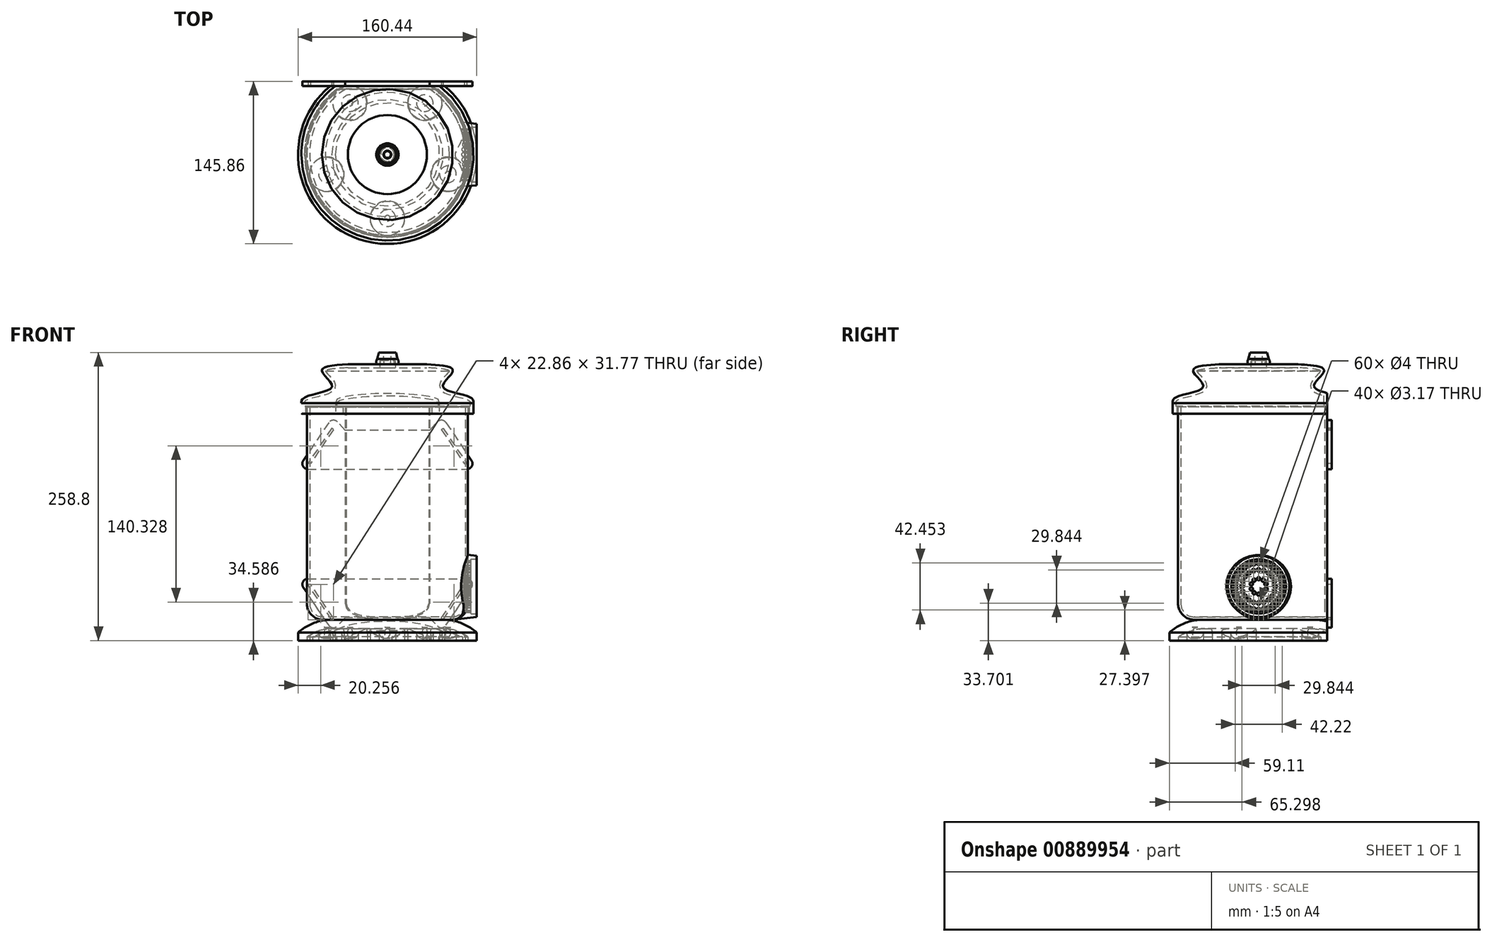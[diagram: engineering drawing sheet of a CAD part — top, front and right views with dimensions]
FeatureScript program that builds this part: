
annotation { "Feature Type Name" : "Feature", "Feature Type Description" : "" }
export const myFeature = defineFeature(function(context is Context, id is Id, definition is map)
    precondition{}
    {
        {
            var Q0;
            Q0=qCreatedBy(makeId("Top.planeOp"),FACE);
            var sketch = newSketch(context, id + "F0", { "sketchPlane" : qUnion([Q0])});
            skCircle(sketch, "E0", {"center": v(0, 0) * mm, "radius": 72.34 * mm});
            skSolve(sketch);
        }
        {
            var Q0;
            Q0=makeQuery(id+"F0.imprint","IMPRINT",FACE,{"disambiguationData":[TD([[makeQuery(id+"F0.imprint","IMPRINT",EDGE,{"derivedFrom":sQuery(id+"F0.wireOp",EDGE,"E0")}),1.0]])]});
            extrude(context, id + "F1", {"entities" : qUnion([Q0]), "depth" : 191 * mm, "offsetDistance" : 25 * mm});
        }
        {
            var Q0;
            Q0=makeQuery(id+"F1.opExtrude","CAP_EDGE",EDGE,{"disambiguationData":[OSD([sQuery(id+"F0.wireOp",EDGE,"E0")])],"isStart":true});
            fillet(context, id + "F2", {"entities" : qUnion([Q0]), "radius" : 14.5 * mm, "tangentPropagation" : true, "allowEdgeOverflow" : false});
        }
        {
            var Q0;
            Q0=qCreatedBy(makeId("Right.planeOp"),FACE);
            var sketch = newSketch(context, id + "F3", { "sketchPlane" : qUnion([Q0])});
            skLineSegment(sketch, "E1", {"start": v(0, 191.62) * mm, "end": v(0, 229.3) * mm});
            skLineSegment(sketch, "E2", {"start": v(0, 229.3) * mm, "end": v(-35.51, 229.3) * mm});
            skFitSpline(sketch, "E3", {"points": [v(-35.51, 229.3) * mm, v(-58.86, 223.46) * mm, v(-49.78, 209.2) * mm, v(-75.72, 198.82) * mm, v(-76.36, 191.62) * mm], "startDerivative": vector(-123.31, -7) * mm, "endDerivative": vector(16.64, -43.35) * mm});
            skLineSegment(sketch, "E4", {"start": v(-77.24, 194.4) * mm, "end": v(-77.24, 184.83) * mm});
            skLineSegment(sketch, "E5", {"start": v(-77.24, 184.83) * mm, "end": v(-73.36, 184.83) * mm});
            skLineSegment(sketch, "E6", {"start": v(-73.36, 184.83) * mm, "end": v(-73.36, 191.62) * mm});
            skLineSegment(sketch, "E7", {"start": v(-73.36, 191.62) * mm, "end": v(0, 191.62) * mm});
            skPoint(sketch, "E8.orphan", {"position": v(4.32, 191.62) * mm});
            skPoint(sketch, "E9.orphan", {"position": v(0, 191.04) * mm});
            skSolve(sketch);
        }
        {
            var Q0;
            Q0=makeQuery(id+"F3.imprint","IMPRINT",FACE,{"disambiguationData":[TD([[makeQuery(id+"F3.imprint","IMPRINT",EDGE,{"derivedFrom":sQuery(id+"F3.wireOp",EDGE,"E1")}),1.0]])]});
            var Q1;
            Q1=sQuery(id+"F3.wireOp",EDGE,"E1");
            revolve(context, id + "F4", {"surfaceOperationType" : NewSurfaceOperationType.NEW, "entities" : qUnion([Q0]), "axis" : qUnion([Q1]), "revolveType" : RevolveType.FULL});
        }
        {
            var Q0;
            Q0=qCreatedBy(makeId("Front.planeOp"),FACE);
            var sketch = newSketch(context, id + "F5", { "sketchPlane" : qUnion([Q0])});
            skLineSegment(sketch, "E10", {"start": v(0, 0) * mm, "end": v(-68.08, 0) * mm});
            skLineSegment(sketch, "E11", {"start": v(-68.08, 0) * mm, "end": v(-80.22, -11.61) * mm});
            skLineSegment(sketch, "E12", {"start": v(-80.22, -11.61) * mm, "end": v(-80.22, -18.75) * mm});
            skLineSegment(sketch, "E13", {"start": v(-80.22, -18.75) * mm, "end": v(0, -18.75) * mm});
            skLineSegment(sketch, "E14", {"start": v(0, -18.75) * mm, "end": v(0, 0) * mm});
            skSolve(sketch);
        }
        {
            var Q0;
            Q0=makeQuery(id+"F5.imprint","IMPRINT",FACE,{"disambiguationData":[TD([[makeQuery(id+"F5.imprint","IMPRINT",EDGE,{"derivedFrom":sQuery(id+"F5.wireOp",EDGE,"E10")}),1.0]])]});
            var Q1;
            Q1=sQuery(id+"F5.wireOp",EDGE,"E14");
            revolve(context, id + "F6", {"surfaceOperationType" : NewSurfaceOperationType.NEW, "entities" : qUnion([Q0]), "axis" : qUnion([Q1]), "revolveType" : RevolveType.FULL});
        }
        {
            var Q0;
            Q0=makeQuery(id+"F6.opRevolve","SWEPT_EDGE",EDGE,{"disambiguationData":[OSD([sQuery(id+"F5.wireOp",EDGE,"E10"),sQuery(id+"F5.wireOp",EDGE,"E11")])]});
            fillet(context, id + "F7", {"entities" : qUnion([Q0]), "radius" : 45.18 * mm, "tangentPropagation" : true, "allowEdgeOverflow" : false});
        }
        {
            var Q0;
            Q0=makeQuery(id+"F6.opRevolve","SWEPT_FACE",FACE,{"disambiguationData":[OSD([sQuery(id+"F5.wireOp",EDGE,"E13")])]});
            var sketch = newSketch(context, id + "F8", { "sketchPlane" : qUnion([Q0])});
            skCircle(sketch, "E15", {"center": v(0, 57.16) * mm, "radius": 7.5 * mm});
            skCircle(sketch, "E16.1.0", {"center": v(-54.36, 17.66) * mm, "radius": 7.5 * mm});
            skCircle(sketch, "E16.2.0", {"center": v(-33.6, -46.24) * mm, "radius": 7.5 * mm});
            skCircle(sketch, "E16.3.0", {"center": v(33.6, -46.24) * mm, "radius": 7.5 * mm});
            skCircle(sketch, "E16.4.0", {"center": v(54.36, 17.66) * mm, "radius": 7.5 * mm});
            skPoint(sketch, "E16.center", {"position": v(0, 0) * mm});
            skSolve(sketch);
        }
        {
            var Q0;
            Q0=makeQuery(id+"F8.imprint","IMPRINT",FACE,{"disambiguationData":[TD([[makeQuery(id+"F8.imprint","IMPRINT",EDGE,{"derivedFrom":sQuery(id+"F8.wireOp",EDGE,"E15")}),1.0]])]});
            var Q1;
            Q1=makeQuery(id+"F8.imprint","IMPRINT",FACE,{"disambiguationData":[TD([[makeQuery(id+"F8.imprint","IMPRINT",EDGE,{"derivedFrom":sQuery(id+"F8.wireOp",EDGE,"E16.4.0")}),1.0]])]});
            var Q2;
            Q2=makeQuery(id+"F8.imprint","IMPRINT",FACE,{"disambiguationData":[TD([[makeQuery(id+"F8.imprint","IMPRINT",EDGE,{"derivedFrom":sQuery(id+"F8.wireOp",EDGE,"E16.3.0")}),1.0]])]});
            var Q3;
            Q3=makeQuery(id+"F8.imprint","IMPRINT",FACE,{"disambiguationData":[TD([[makeQuery(id+"F8.imprint","IMPRINT",EDGE,{"derivedFrom":sQuery(id+"F8.wireOp",EDGE,"E16.2.0")}),1.0]])]});
            var Q4;
            Q4=makeQuery(id+"F8.imprint","IMPRINT",FACE,{"disambiguationData":[TD([[makeQuery(id+"F8.imprint","IMPRINT",EDGE,{"derivedFrom":sQuery(id+"F8.wireOp",EDGE,"E16.1.0")}),1.0]])]});
            extrude(context, id + "F9", {"entities" : qUnion([Q0, Q1, Q2, Q3, Q4]), "operationType" : NewBodyOperationType.REMOVE, "oppositeDirection" : true, "depth" : 12 * mm, "offsetDistance" : 25 * mm});
        }
        {
            var Q0;
            Q0=makeQuery(id+"F9.boolean.opBoolean","COPY",EDGE,{"derivedFrom":makeQuery(id+"F9.opExtrude","CAP_EDGE",EDGE,{"disambiguationData":[OSD([sQuery(id+"F8.wireOp",EDGE,"E16.2.0")])],"isStart":false})});
            var Q1;
            Q1=makeQuery(id+"F9.boolean.opBoolean","COPY",EDGE,{"derivedFrom":makeQuery(id+"F9.opExtrude","CAP_EDGE",EDGE,{"disambiguationData":[OSD([sQuery(id+"F8.wireOp",EDGE,"E16.1.0")])],"isStart":false})});
            var Q2;
            Q2=makeQuery(id+"F9.boolean.opBoolean","COPY",EDGE,{"derivedFrom":makeQuery(id+"F9.opExtrude","CAP_EDGE",EDGE,{"disambiguationData":[OSD([sQuery(id+"F8.wireOp",EDGE,"E15")])],"isStart":false})});
            var Q3;
            Q3=makeQuery(id+"F9.boolean.opBoolean","COPY",EDGE,{"derivedFrom":makeQuery(id+"F9.opExtrude","CAP_EDGE",EDGE,{"disambiguationData":[OSD([sQuery(id+"F8.wireOp",EDGE,"E16.3.0")])],"isStart":false})});
            var Q4;
            Q4=makeQuery(id+"F9.boolean.opBoolean","COPY",EDGE,{"derivedFrom":makeQuery(id+"F9.opExtrude","CAP_EDGE",EDGE,{"disambiguationData":[OSD([sQuery(id+"F8.wireOp",EDGE,"E16.4.0")])],"isStart":false})});
            fillet(context, id + "F10", {"entities" : qUnion([Q0, Q1, Q2, Q3, Q4]), "radius" : 5 * mm, "tangentPropagation" : true, "allowEdgeOverflow" : false});
        }
        {
            var Q0;
            Q0=makeQuery(id+"F6.opRevolve","SWEPT_FACE",FACE,{"disambiguationData":[OSD([sQuery(id+"F5.wireOp",EDGE,"E13")])]});
            shell(context, id + "F11", {"entities" : qUnion([Q0]), "thickness" : 8 * mm});
        }
        {
            var Q0;
            Q0=qCreatedBy(makeId("Top.planeOp"),FACE);
            var sketch = newSketch(context, id + "F12", { "sketchPlane" : qUnion([Q0])});
            skLineSegment(sketch, "E17.bottom", {"start": v(-88.63, 123.42) * mm, "end": v(97.23, 123.42) * mm});
            skLineSegment(sketch, "E17.top", {"start": v(-88.63, 61.64) * mm, "end": v(97.23, 61.64) * mm});
            skLineSegment(sketch, "E17.left", {"start": v(-88.63, 123.42) * mm, "end": v(-88.63, 61.64) * mm});
            skLineSegment(sketch, "E17.right", {"start": v(97.23, 123.42) * mm, "end": v(97.23, 61.64) * mm});
            skSolve(sketch);
        }
        {
            var Q0;
            Q0=makeQuery(id+"F12.imprint","IMPRINT",FACE,{"disambiguationData":[TD([[makeQuery(id+"F12.imprint","IMPRINT",EDGE,{"derivedFrom":sQuery(id+"F12.wireOp",EDGE,"E17.bottom")}),-1.0]])]});
            extrude(context, id + "F13", {"entities" : qUnion([Q0]), "operationType" : NewBodyOperationType.REMOVE, "endBound" : BoundingType.THROUGH_ALL, "depth" : 564 * mm, "offsetDistance" : 25 * mm, "hasSecondDirection" : true, "secondDirectionOppositeDirection" : true, "secondDirectionDepth" : 25 * mm});
        }
        {
            var Q0;
            {var subQ0=sQuery(id+"F0.wireOp",EDGE,"E0");Q0=makeQuery(id+"F13.boolean.opBoolean","COPY",FACE,{"disambiguationData":[TD([makeQuery(id+"F1.opExtrude","SWEPT_FACE",FACE,{"disambiguationData":[OSD([subQ0])]})])],"derivedFrom":makeQuery(id+"F13.opExtrude","SWEPT_FACE",FACE,{"disambiguationData":[OSD([sQuery(id+"F12.wireOp",EDGE,"E17.top")])]})});}
            var sketch = newSketch(context, id + "F14", { "sketchPlane" : qUnion([Q0])});
            skLineSegment(sketch, "E18.bottom", {"start": v(80.8, 135.28) * mm, "end": v(-80.8, 135.28) * mm});
            skPoint(sketch, "E18.middle", {"position": v(0, 158.7) * mm});
            skLineSegment(sketch, "E19", {"start": v(-37.86, 170.21) * mm, "end": v(37.86, 170.21) * mm});
            skLineSegment(sketch, "E20", {"start": v(37.86, 170.21) * mm, "end": v(49.17, 182.13) * mm});
            skLineSegment(sketch, "E21", {"start": v(49.17, 182.13) * mm, "end": v(80.8, 135.28) * mm});
            skPoint(sketch, "E18.left.end.orphan", {"position": v(80.8, 182.13) * mm});
            skLineSegment(sketch, "E22.MirrorCS", {"start": v(-49.17, 182.13) * mm, "end": v(-80.8, 135.28) * mm});
            skLineSegment(sketch, "E23.MirrorCS", {"start": v(-37.86, 170.21) * mm, "end": v(-49.17, 182.13) * mm});
            skPoint(sketch, "E24.orphan", {"position": v(-80.8, 182.13) * mm});
            skLineSegment(sketch, "E25.0", {"start": v(-48.54, 170.56) * mm, "end": v(-49.95, 172.05) * mm});
            skLineSegment(sketch, "E26.0", {"start": v(80.8, 140.28) * mm, "end": v(77.42, 140.28) * mm});
            skLineSegment(sketch, "E27.trimOffspring", {"start": v(-48.54, 170.56) * mm, "end": v(-68.98, 140.28) * mm});
            skLineSegment(sketch, "E28.trimOffspring", {"start": v(-49.95, 172.05) * mm, "end": v(-71.4, 140.28) * mm});
            skLineSegment(sketch, "E29.trimOffspring", {"start": v(-68.98, 140.28) * mm, "end": v(-71.4, 140.28) * mm});
            skLineSegment(sketch, "E30.MirrorCS", {"start": v(48.54, 170.56) * mm, "end": v(68.98, 140.28) * mm});
            skLineSegment(sketch, "E31.MirrorCS", {"start": v(49.95, 172.05) * mm, "end": v(71.4, 140.28) * mm});
            skLineSegment(sketch, "E32.MirrorCS", {"start": v(48.54, 170.56) * mm, "end": v(49.95, 172.05) * mm});
            skLineSegment(sketch, "E33.MirrorCS", {"start": v(68.98, 140.28) * mm, "end": v(71.4, 140.28) * mm});
            skSolve(sketch);
        }
        {
            var Q0;
            {var subQ7=sQuery(id+"F14.wireOp",EDGE,"E19");Q0=makeQuery(id+"F14.imprint","IMPRINT",FACE,{"disambiguationData":[TD([[makeQuery(id+"F14.imprint","IMPRINT",EDGE,{"derivedFrom":subQ7}),-1.0]])]});}
            var Q1;
            {var subQ4=sQuery(id+"F14.wireOp",EDGE,"E20");Q1=makeQuery(id+"F14.imprint","IMPRINT",FACE,{"disambiguationData":[TD([[makeQuery(id+"F14.imprint","IMPRINT",EDGE,{"derivedFrom":subQ4}),-1.0]])]});}
            var Q2;
            {var subQ1=sQuery(id+"F14.wireOp",EDGE,"E22.MirrorCS");Q2=makeQuery(id+"F14.imprint","IMPRINT",FACE,{"disambiguationData":[TD([[makeQuery(id+"F14.imprint","IMPRINT",EDGE,{"derivedFrom":subQ1}),1.0]])]});}
            extrude(context, id + "F15", {"entities" : qUnion([Q0, Q1, Q2]), "depth" : 4 * mm, "offsetDistance" : 25 * mm});
        }
        {
            var Q0;
            Q0=makeQuery(id+"F15.opExtrude","SWEPT_EDGE",EDGE,{"disambiguationData":[OSD([sQuery(id+"F14.wireOp",EDGE,"E18.bottom"),sQuery(id+"F14.wireOp",EDGE,"E22.MirrorCS")])]});
            var Q1;
            Q1=makeQuery(id+"F15.opExtrude","SWEPT_EDGE",EDGE,{"disambiguationData":[OSD([sQuery(id+"F14.wireOp",EDGE,"E18.bottom"),sQuery(id+"F14.wireOp",EDGE,"E21")])]});
            var Q2;
            Q2=makeQuery(id+"F15.opExtrude","SWEPT_EDGE",EDGE,{"disambiguationData":[OSD([sQuery(id+"F14.wireOp",EDGE,"E20"),sQuery(id+"F14.wireOp",EDGE,"E21")])]});
            var Q3;
            Q3=makeQuery(id+"F15.opExtrude","SWEPT_EDGE",EDGE,{"disambiguationData":[OSD([sQuery(id+"F14.wireOp",EDGE,"E22.MirrorCS"),sQuery(id+"F14.wireOp",EDGE,"E23.MirrorCS")])]});
            fillet(context, id + "F16", {"entities" : qUnion([Q0, Q1, Q2, Q3]), "radius" : 5 * mm, "tangentPropagation" : true, "allowEdgeOverflow" : false});
        }
        {
            var Q0;
            Q0=qCreatedBy(makeId("Top.planeOp"),FACE);
            cPlane(context, id + "F17", {"entities" : qUnion([Q0]), "cplaneType" : CPlaneType.OFFSET, "offset" : 86 * mm, "width" : 150 * mm, "height" : 150 * mm});
        }
        {
            var Q0;
            Q0=makeQuery(id+"F15.opExtrude","SWEPT_BODY",BODY,{"disambiguationData":[OSD([sQuery(id+"F14.wireOp",EDGE,"E18.bottom"),sQuery(id+"F14.wireOp",EDGE,"E19"),sQuery(id+"F14.wireOp",EDGE,"E20"),sQuery(id+"F14.wireOp",EDGE,"E21"),sQuery(id+"F14.wireOp",EDGE,"E22.MirrorCS"),sQuery(id+"F14.wireOp",EDGE,"E23.MirrorCS"),sQuery(id+"F14.wireOp",EDGE,"E25.0"),sQuery(id+"F14.wireOp",EDGE,"E27.trimOffspring"),sQuery(id+"F14.wireOp",EDGE,"E28.trimOffspring"),sQuery(id+"F14.wireOp",EDGE,"E29.trimOffspring"),sQuery(id+"F14.wireOp",EDGE,"E30.MirrorCS"),sQuery(id+"F14.wireOp",EDGE,"E31.MirrorCS"),sQuery(id+"F14.wireOp",EDGE,"E32.MirrorCS"),sQuery(id+"F14.wireOp",EDGE,"E33.MirrorCS")])]});
            var Q1;
            Q1=qCreatedBy(id+"F17.planeOp",FACE);
            mirror(context, id + "F18", {"entities" : qUnion([Q0]), "mirrorPlane" : qUnion([Q1])});
        }
        {
            var Q0;
            Q0=qCreatedBy(makeId("Front.planeOp"),FACE);
            var sketch = newSketch(context, id + "F19", { "sketchPlane" : qUnion([Q0])});
            skLineSegment(sketch, "E34", {"start": v(10, 231.46) * mm, "end": v(10, 225.67) * mm});
            skLineSegment(sketch, "E35", {"start": v(10, 225.67) * mm, "end": v(3, 225.67) * mm});
            skLineSegment(sketch, "E36", {"start": v(3, 225.67) * mm, "end": v(3, 228.82) * mm});
            skArc(sketch, "E37.filletArc", {"start": v(10, 231.46) * mm, "mid": v(9.8, 232.9) * mm, "end": v(9.18, 234.2) * mm});
            skLineSegment(sketch, "E38", {"start": v(3, 228.82) * mm, "end": v(3.54, 240.05) * mm});
            skLineSegment(sketch, "E39", {"start": v(0, 228.43) * mm, "end": v(0, 255.57) * mm, "construction": true});
            skLineSegment(sketch, "E40", {"start": v(9.18, 234.2) * mm, "end": v(7.68, 240.05) * mm});
            skLineSegment(sketch, "E41", {"start": v(7.68, 240.05) * mm, "end": v(3.54, 240.05) * mm});
            skSolve(sketch);
        }
        {
            var Q0;
            Q0=makeQuery(id+"F19.imprint","IMPRINT",FACE,{"disambiguationData":[TD([[makeQuery(id+"F19.imprint","IMPRINT",EDGE,{"derivedFrom":sQuery(id+"F19.wireOp",EDGE,"E34")}),-1.0]])]});
            var Q1;
            Q1=sQuery(id+"F19.wireOp",EDGE,"E39");
            revolve(context, id + "F20", {"operationType" : NewBodyOperationType.ADD, "surfaceOperationType" : NewSurfaceOperationType.NEW, "entities" : qUnion([Q0]), "axis" : qUnion([Q1]), "revolveType" : RevolveType.FULL});
        }
        {
            var Q0;
            Q0=makeQuery(id+"F20.boolean.opBoolean","SPLIT",FACE,{"disambiguationData":[TD([makeQuery(id+"F20.opRevolve","SWEPT_FACE",FACE,{"disambiguationData":[OSD([sQuery(id+"F19.wireOp",EDGE,"E38")])]})])],"derivedFrom":makeQuery(id+"F4.opRevolve","SWEPT_FACE",FACE,{"disambiguationData":[OSD([sQuery(id+"F3.wireOp",EDGE,"E2")])]})});
            var Q1;
            Q1=makeQuery(id+"F4.opRevolve","SWEPT_FACE",FACE,{"disambiguationData":[OSD([sQuery(id+"F3.wireOp",EDGE,"E7")])]});
            shell(context, id + "F21", {"entities" : qUnion([Q0, Q1]), "thickness" : 3 * mm});
        }
        {
            var Q0;
            Q0=makeQuery(id+"F1.opExtrude","CAP_FACE",FACE,{"disambiguationData":[OSD([sQuery(id+"F0.wireOp",EDGE,"E0")])],"isStart":false});
            shell(context, id + "F22", {"entities" : qUnion([Q0]), "thickness" : 2.5 * mm});
        }
        {
            var Q0;
            Q0=qCreatedBy(makeId("Right.planeOp"),FACE);
            cPlane(context, id + "F23", {"entities" : qUnion([Q0]), "cplaneType" : CPlaneType.OFFSET, "offset" : 80 * mm, "width" : 150 * mm, "height" : 150 * mm});
        }
        {
            var Q0;
            Q0=qCreatedBy(id+"F23.planeOp",FACE);
            var sketch = newSketch(context, id + "F24", { "sketchPlane" : qUnion([Q0])});
            skCircle(sketch, "E42", {"center": v(0, 29.87) * mm, "radius": 27.58 * mm});
            skSolve(sketch);
        }
        {
            var Q0;
            Q0=makeQuery(id+"F24.imprint","IMPRINT",FACE,{"disambiguationData":[TD([[makeQuery(id+"F24.imprint","IMPRINT",EDGE,{"derivedFrom":sQuery(id+"F24.wireOp",EDGE,"E42")}),1.0]])]});
            extrude(context, id + "F25", {"entities" : qUnion([Q0]), "endBound" : BoundingType.UP_TO_NEXT, "oppositeDirection" : true, "depth" : 25 * mm, "offsetDistance" : 25 * mm, "hasDraft" : true, "draftAngle" : 6 * degree});
        }
        {
            var Q0;
            Q0=makeQuery(id+"F25.opExtrude","CAP_FACE",FACE,{"disambiguationData":[OSD([sQuery(id+"F24.wireOp",EDGE,"E42")])],"isStart":true});
            var sketch = newSketch(context, id + "F26", { "sketchPlane" : qUnion([Q0])});
            skCircle(sketch, "E43.0", {"center": v(0, 29.87) * mm, "radius": 24.58 * mm});
            skPoint(sketch, "E44.orphan", {"position": v(0, 54.45) * mm});
            skCircle(sketch, "E45", {"center": v(0, 51.1) * mm, "radius": 2 * mm});
            skCircle(sketch, "E46.1.0", {"center": v(-4.41, 50.64) * mm, "radius": 2 * mm});
            skCircle(sketch, "E46.2.0", {"center": v(-8.63, 49.26) * mm, "radius": 2 * mm});
            skCircle(sketch, "E46.3.0", {"center": v(-12.48, 47.05) * mm, "radius": 2 * mm});
            skCircle(sketch, "E46.4.0", {"center": v(-15.77, 44.08) * mm, "radius": 2 * mm});
            skCircle(sketch, "E46.5.0", {"center": v(-18.38, 40.49) * mm, "radius": 2 * mm});
            skCircle(sketch, "E46.6.0", {"center": v(-20.19, 36.43) * mm, "radius": 2 * mm});
            skCircle(sketch, "E46.7.0", {"center": v(-21.11, 32.1) * mm, "radius": 2 * mm});
            skCircle(sketch, "E46.8.0", {"center": v(-21.11, 27.65) * mm, "radius": 2 * mm});
            skCircle(sketch, "E46.9.0", {"center": v(-20.19, 23.31) * mm, "radius": 2 * mm});
            skCircle(sketch, "E46.10.0", {"center": v(-18.38, 19.26) * mm, "radius": 2 * mm});
            skCircle(sketch, "E46.11.0", {"center": v(-15.77, 15.67) * mm, "radius": 2 * mm});
            skCircle(sketch, "E46.12.0", {"center": v(-12.48, 12.7) * mm, "radius": 2 * mm});
            skCircle(sketch, "E46.13.0", {"center": v(-8.63, 10.48) * mm, "radius": 2 * mm});
            skCircle(sketch, "E46.14.0", {"center": v(-4.41, 9.11) * mm, "radius": 2 * mm});
            skCircle(sketch, "E46.15.0", {"center": v(0, 8.65) * mm, "radius": 2 * mm});
            skCircle(sketch, "E46.16.0", {"center": v(4.41, 9.11) * mm, "radius": 2 * mm});
            skCircle(sketch, "E46.17.0", {"center": v(8.63, 10.48) * mm, "radius": 2 * mm});
            skCircle(sketch, "E46.18.0", {"center": v(12.48, 12.7) * mm, "radius": 2 * mm});
            skCircle(sketch, "E46.19.0", {"center": v(15.77, 15.67) * mm, "radius": 2 * mm});
            skCircle(sketch, "E46.20.0", {"center": v(18.38, 19.26) * mm, "radius": 2 * mm});
            skCircle(sketch, "E46.21.0", {"center": v(20.19, 23.31) * mm, "radius": 2 * mm});
            skCircle(sketch, "E46.22.0", {"center": v(21.11, 27.65) * mm, "radius": 2 * mm});
            skCircle(sketch, "E46.23.0", {"center": v(21.11, 32.1) * mm, "radius": 2 * mm});
            skCircle(sketch, "E46.24.0", {"center": v(20.19, 36.43) * mm, "radius": 2 * mm});
            skCircle(sketch, "E46.25.0", {"center": v(18.38, 40.49) * mm, "radius": 2 * mm});
            skCircle(sketch, "E46.26.0", {"center": v(15.77, 44.08) * mm, "radius": 2 * mm});
            skCircle(sketch, "E46.27.0", {"center": v(12.48, 47.05) * mm, "radius": 2 * mm});
            skCircle(sketch, "E46.28.0", {"center": v(8.63, 49.26) * mm, "radius": 2 * mm});
            skCircle(sketch, "E46.29.0", {"center": v(4.41, 50.64) * mm, "radius": 2 * mm});
            skCircle(sketch, "E47", {"center": v(0, 44.8) * mm, "radius": 1.58 * mm});
            skCircle(sketch, "E48", {"center": v(0, 36.84) * mm, "radius": 1.52 * mm});
            skCircle(sketch, "E49.1.0", {"center": v(-4.61, 44.07) * mm, "radius": 1.58 * mm});
            skCircle(sketch, "E49.2.0", {"center": v(-8.77, 41.95) * mm, "radius": 1.58 * mm});
            skCircle(sketch, "E49.3.0", {"center": v(-12.07, 38.64) * mm, "radius": 1.58 * mm});
            skCircle(sketch, "E49.4.0", {"center": v(-14.2, 34.48) * mm, "radius": 1.58 * mm});
            skCircle(sketch, "E49.5.0", {"center": v(-14.92, 29.87) * mm, "radius": 1.58 * mm});
            skCircle(sketch, "E49.6.0", {"center": v(-14.2, 25.26) * mm, "radius": 1.58 * mm});
            skCircle(sketch, "E49.7.0", {"center": v(-12.07, 21.1) * mm, "radius": 1.58 * mm});
            skCircle(sketch, "E49.8.0", {"center": v(-8.77, 17.8) * mm, "radius": 1.58 * mm});
            skCircle(sketch, "E49.9.0", {"center": v(-4.61, 15.68) * mm, "radius": 1.58 * mm});
            skCircle(sketch, "E49.10.0", {"center": v(0, 14.95) * mm, "radius": 1.58 * mm});
            skCircle(sketch, "E49.11.0", {"center": v(4.61, 15.68) * mm, "radius": 1.58 * mm});
            skCircle(sketch, "E49.12.0", {"center": v(8.77, 17.8) * mm, "radius": 1.58 * mm});
            skCircle(sketch, "E49.13.0", {"center": v(12.07, 21.1) * mm, "radius": 1.58 * mm});
            skCircle(sketch, "E49.14.0", {"center": v(14.2, 25.26) * mm, "radius": 1.58 * mm});
            skCircle(sketch, "E49.15.0", {"center": v(14.92, 29.87) * mm, "radius": 1.58 * mm});
            skCircle(sketch, "E49.16.0", {"center": v(14.2, 34.48) * mm, "radius": 1.58 * mm});
            skCircle(sketch, "E49.17.0", {"center": v(12.07, 38.64) * mm, "radius": 1.58 * mm});
            skCircle(sketch, "E49.18.0", {"center": v(8.77, 41.95) * mm, "radius": 1.58 * mm});
            skCircle(sketch, "E49.19.0", {"center": v(4.61, 44.07) * mm, "radius": 1.58 * mm});
            skCircle(sketch, "E50.1.0", {"center": v(-4.1, 35.5) * mm, "radius": 1.52 * mm});
            skCircle(sketch, "E50.2.0", {"center": v(-6.62, 32.03) * mm, "radius": 1.52 * mm});
            skCircle(sketch, "E50.3.0", {"center": v(-6.62, 27.72) * mm, "radius": 1.52 * mm});
            skCircle(sketch, "E50.4.0", {"center": v(-4.1, 24.24) * mm, "radius": 1.52 * mm});
            skCircle(sketch, "E50.5.0", {"center": v(0, 22.9) * mm, "radius": 1.52 * mm});
            skCircle(sketch, "E50.6.0", {"center": v(4.1, 24.24) * mm, "radius": 1.52 * mm});
            skCircle(sketch, "E50.7.0", {"center": v(6.62, 27.72) * mm, "radius": 1.52 * mm});
            skCircle(sketch, "E50.8.0", {"center": v(6.62, 32.03) * mm, "radius": 1.52 * mm});
            skCircle(sketch, "E50.9.0", {"center": v(4.1, 35.5) * mm, "radius": 1.52 * mm});
            skSolve(sketch);
        }
        {
            var Q0;
            Q0=makeQuery(id+"F26.imprint","IMPRINT",FACE,{"disambiguationData":[TD([[makeQuery(id+"F26.imprint","IMPRINT",EDGE,{"derivedFrom":sQuery(id+"F26.wireOp",EDGE,"E43.0")}),1.0]])]});
            extrude(context, id + "F27", {"entities" : qUnion([Q0]), "operationType" : NewBodyOperationType.REMOVE, "oppositeDirection" : true, "depth" : 5 * mm, "offsetDistance" : 25 * mm});
        }
        {
            var Q0;
            Q0=makeQuery(id+"F27.boolean.opBoolean","SPLIT",FACE,{"disambiguationData":[TD([makeQuery(id+"F27.opExtrude","SWEPT_FACE",FACE,{"disambiguationData":[OSD([sQuery(id+"F26.wireOp",EDGE,"E46.8.0")])]})])],"derivedFrom":makeQuery(id+"F25.opExtrude","CAP_FACE",FACE,{"disambiguationData":[OSD([sQuery(id+"F24.wireOp",EDGE,"E42")])],"isStart":true})});
            var Q1;
            Q1=makeQuery(id+"F27.boolean.opBoolean","SPLIT",FACE,{"disambiguationData":[TD([makeQuery(id+"F27.opExtrude","SWEPT_FACE",FACE,{"disambiguationData":[OSD([sQuery(id+"F26.wireOp",EDGE,"E46.7.0")])]})])],"derivedFrom":makeQuery(id+"F25.opExtrude","CAP_FACE",FACE,{"disambiguationData":[OSD([sQuery(id+"F24.wireOp",EDGE,"E42")])],"isStart":true})});
            var Q2;
            Q2=makeQuery(id+"F27.boolean.opBoolean","SPLIT",FACE,{"disambiguationData":[TD([makeQuery(id+"F27.opExtrude","SWEPT_FACE",FACE,{"disambiguationData":[OSD([sQuery(id+"F26.wireOp",EDGE,"E46.6.0")])]})])],"derivedFrom":makeQuery(id+"F25.opExtrude","CAP_FACE",FACE,{"disambiguationData":[OSD([sQuery(id+"F24.wireOp",EDGE,"E42")])],"isStart":true})});
            var Q3;
            Q3=makeQuery(id+"F27.boolean.opBoolean","SPLIT",FACE,{"disambiguationData":[TD([makeQuery(id+"F27.opExtrude","SWEPT_FACE",FACE,{"disambiguationData":[OSD([sQuery(id+"F26.wireOp",EDGE,"E46.5.0")])]})])],"derivedFrom":makeQuery(id+"F25.opExtrude","CAP_FACE",FACE,{"disambiguationData":[OSD([sQuery(id+"F24.wireOp",EDGE,"E42")])],"isStart":true})});
            var Q4;
            Q4=makeQuery(id+"F27.boolean.opBoolean","SPLIT",FACE,{"disambiguationData":[TD([makeQuery(id+"F27.opExtrude","SWEPT_FACE",FACE,{"disambiguationData":[OSD([sQuery(id+"F26.wireOp",EDGE,"E46.4.0")])]})])],"derivedFrom":makeQuery(id+"F25.opExtrude","CAP_FACE",FACE,{"disambiguationData":[OSD([sQuery(id+"F24.wireOp",EDGE,"E42")])],"isStart":true})});
            var Q5;
            Q5=makeQuery(id+"F27.boolean.opBoolean","SPLIT",FACE,{"disambiguationData":[TD([makeQuery(id+"F27.opExtrude","SWEPT_FACE",FACE,{"disambiguationData":[OSD([sQuery(id+"F26.wireOp",EDGE,"E46.3.0")])]})])],"derivedFrom":makeQuery(id+"F25.opExtrude","CAP_FACE",FACE,{"disambiguationData":[OSD([sQuery(id+"F24.wireOp",EDGE,"E42")])],"isStart":true})});
            var Q6;
            Q6=makeQuery(id+"F27.boolean.opBoolean","SPLIT",FACE,{"disambiguationData":[TD([makeQuery(id+"F27.opExtrude","SWEPT_FACE",FACE,{"disambiguationData":[OSD([sQuery(id+"F26.wireOp",EDGE,"E46.2.0")])]})])],"derivedFrom":makeQuery(id+"F25.opExtrude","CAP_FACE",FACE,{"disambiguationData":[OSD([sQuery(id+"F24.wireOp",EDGE,"E42")])],"isStart":true})});
            var Q7;
            Q7=makeQuery(id+"F27.boolean.opBoolean","SPLIT",FACE,{"disambiguationData":[TD([makeQuery(id+"F27.opExtrude","SWEPT_FACE",FACE,{"disambiguationData":[OSD([sQuery(id+"F26.wireOp",EDGE,"E46.1.0")])]})])],"derivedFrom":makeQuery(id+"F25.opExtrude","CAP_FACE",FACE,{"disambiguationData":[OSD([sQuery(id+"F24.wireOp",EDGE,"E42")])],"isStart":true})});
            var Q8;
            Q8=makeQuery(id+"F27.boolean.opBoolean","SPLIT",FACE,{"disambiguationData":[TD([makeQuery(id+"F27.opExtrude","SWEPT_FACE",FACE,{"disambiguationData":[OSD([sQuery(id+"F26.wireOp",EDGE,"E45")])]})])],"derivedFrom":makeQuery(id+"F25.opExtrude","CAP_FACE",FACE,{"disambiguationData":[OSD([sQuery(id+"F24.wireOp",EDGE,"E42")])],"isStart":true})});
            var Q9;
            Q9=makeQuery(id+"F27.boolean.opBoolean","SPLIT",FACE,{"disambiguationData":[TD([makeQuery(id+"F27.opExtrude","SWEPT_FACE",FACE,{"disambiguationData":[OSD([sQuery(id+"F26.wireOp",EDGE,"E46.29.0")])]})])],"derivedFrom":makeQuery(id+"F25.opExtrude","CAP_FACE",FACE,{"disambiguationData":[OSD([sQuery(id+"F24.wireOp",EDGE,"E42")])],"isStart":true})});
            var Q10;
            Q10=makeQuery(id+"F27.boolean.opBoolean","SPLIT",FACE,{"disambiguationData":[TD([makeQuery(id+"F27.opExtrude","SWEPT_FACE",FACE,{"disambiguationData":[OSD([sQuery(id+"F26.wireOp",EDGE,"E46.28.0")])]})])],"derivedFrom":makeQuery(id+"F25.opExtrude","CAP_FACE",FACE,{"disambiguationData":[OSD([sQuery(id+"F24.wireOp",EDGE,"E42")])],"isStart":true})});
            var Q11;
            Q11=makeQuery(id+"F27.boolean.opBoolean","SPLIT",FACE,{"disambiguationData":[TD([makeQuery(id+"F27.opExtrude","SWEPT_FACE",FACE,{"disambiguationData":[OSD([sQuery(id+"F26.wireOp",EDGE,"E46.27.0")])]})])],"derivedFrom":makeQuery(id+"F25.opExtrude","CAP_FACE",FACE,{"disambiguationData":[OSD([sQuery(id+"F24.wireOp",EDGE,"E42")])],"isStart":true})});
            var Q12;
            Q12=makeQuery(id+"F27.boolean.opBoolean","SPLIT",FACE,{"disambiguationData":[TD([makeQuery(id+"F27.opExtrude","SWEPT_FACE",FACE,{"disambiguationData":[OSD([sQuery(id+"F26.wireOp",EDGE,"E46.26.0")])]})])],"derivedFrom":makeQuery(id+"F25.opExtrude","CAP_FACE",FACE,{"disambiguationData":[OSD([sQuery(id+"F24.wireOp",EDGE,"E42")])],"isStart":true})});
            var Q13;
            Q13=makeQuery(id+"F27.boolean.opBoolean","SPLIT",FACE,{"disambiguationData":[TD([makeQuery(id+"F27.opExtrude","SWEPT_FACE",FACE,{"disambiguationData":[OSD([sQuery(id+"F26.wireOp",EDGE,"E46.25.0")])]})])],"derivedFrom":makeQuery(id+"F25.opExtrude","CAP_FACE",FACE,{"disambiguationData":[OSD([sQuery(id+"F24.wireOp",EDGE,"E42")])],"isStart":true})});
            var Q14;
            Q14=makeQuery(id+"F27.boolean.opBoolean","SPLIT",FACE,{"disambiguationData":[TD([makeQuery(id+"F27.opExtrude","SWEPT_FACE",FACE,{"disambiguationData":[OSD([sQuery(id+"F26.wireOp",EDGE,"E46.24.0")])]})])],"derivedFrom":makeQuery(id+"F25.opExtrude","CAP_FACE",FACE,{"disambiguationData":[OSD([sQuery(id+"F24.wireOp",EDGE,"E42")])],"isStart":true})});
            var Q15;
            Q15=makeQuery(id+"F27.boolean.opBoolean","SPLIT",FACE,{"disambiguationData":[TD([makeQuery(id+"F27.opExtrude","SWEPT_FACE",FACE,{"disambiguationData":[OSD([sQuery(id+"F26.wireOp",EDGE,"E46.23.0")])]})])],"derivedFrom":makeQuery(id+"F25.opExtrude","CAP_FACE",FACE,{"disambiguationData":[OSD([sQuery(id+"F24.wireOp",EDGE,"E42")])],"isStart":true})});
            var Q16;
            Q16=makeQuery(id+"F27.boolean.opBoolean","SPLIT",FACE,{"disambiguationData":[TD([makeQuery(id+"F27.opExtrude","SWEPT_FACE",FACE,{"disambiguationData":[OSD([sQuery(id+"F26.wireOp",EDGE,"E46.22.0")])]})])],"derivedFrom":makeQuery(id+"F25.opExtrude","CAP_FACE",FACE,{"disambiguationData":[OSD([sQuery(id+"F24.wireOp",EDGE,"E42")])],"isStart":true})});
            var Q17;
            Q17=makeQuery(id+"F27.boolean.opBoolean","SPLIT",FACE,{"disambiguationData":[TD([makeQuery(id+"F27.opExtrude","SWEPT_FACE",FACE,{"disambiguationData":[OSD([sQuery(id+"F26.wireOp",EDGE,"E46.21.0")])]})])],"derivedFrom":makeQuery(id+"F25.opExtrude","CAP_FACE",FACE,{"disambiguationData":[OSD([sQuery(id+"F24.wireOp",EDGE,"E42")])],"isStart":true})});
            var Q18;
            Q18=makeQuery(id+"F27.boolean.opBoolean","SPLIT",FACE,{"disambiguationData":[TD([makeQuery(id+"F27.opExtrude","SWEPT_FACE",FACE,{"disambiguationData":[OSD([sQuery(id+"F26.wireOp",EDGE,"E46.20.0")])]})])],"derivedFrom":makeQuery(id+"F25.opExtrude","CAP_FACE",FACE,{"disambiguationData":[OSD([sQuery(id+"F24.wireOp",EDGE,"E42")])],"isStart":true})});
            var Q19;
            Q19=makeQuery(id+"F27.boolean.opBoolean","SPLIT",FACE,{"disambiguationData":[TD([makeQuery(id+"F27.opExtrude","SWEPT_FACE",FACE,{"disambiguationData":[OSD([sQuery(id+"F26.wireOp",EDGE,"E46.19.0")])]})])],"derivedFrom":makeQuery(id+"F25.opExtrude","CAP_FACE",FACE,{"disambiguationData":[OSD([sQuery(id+"F24.wireOp",EDGE,"E42")])],"isStart":true})});
            var Q20;
            Q20=makeQuery(id+"F27.boolean.opBoolean","SPLIT",FACE,{"disambiguationData":[TD([makeQuery(id+"F27.opExtrude","SWEPT_FACE",FACE,{"disambiguationData":[OSD([sQuery(id+"F26.wireOp",EDGE,"E46.18.0")])]})])],"derivedFrom":makeQuery(id+"F25.opExtrude","CAP_FACE",FACE,{"disambiguationData":[OSD([sQuery(id+"F24.wireOp",EDGE,"E42")])],"isStart":true})});
            var Q21;
            Q21=makeQuery(id+"F27.boolean.opBoolean","SPLIT",FACE,{"disambiguationData":[TD([makeQuery(id+"F27.opExtrude","SWEPT_FACE",FACE,{"disambiguationData":[OSD([sQuery(id+"F26.wireOp",EDGE,"E46.17.0")])]})])],"derivedFrom":makeQuery(id+"F25.opExtrude","CAP_FACE",FACE,{"disambiguationData":[OSD([sQuery(id+"F24.wireOp",EDGE,"E42")])],"isStart":true})});
            var Q22;
            Q22=makeQuery(id+"F27.boolean.opBoolean","SPLIT",FACE,{"disambiguationData":[TD([makeQuery(id+"F27.opExtrude","SWEPT_FACE",FACE,{"disambiguationData":[OSD([sQuery(id+"F26.wireOp",EDGE,"E46.16.0")])]})])],"derivedFrom":makeQuery(id+"F25.opExtrude","CAP_FACE",FACE,{"disambiguationData":[OSD([sQuery(id+"F24.wireOp",EDGE,"E42")])],"isStart":true})});
            var Q23;
            Q23=makeQuery(id+"F27.boolean.opBoolean","SPLIT",FACE,{"disambiguationData":[TD([makeQuery(id+"F27.opExtrude","SWEPT_FACE",FACE,{"disambiguationData":[OSD([sQuery(id+"F26.wireOp",EDGE,"E46.15.0")])]})])],"derivedFrom":makeQuery(id+"F25.opExtrude","CAP_FACE",FACE,{"disambiguationData":[OSD([sQuery(id+"F24.wireOp",EDGE,"E42")])],"isStart":true})});
            var Q24;
            Q24=makeQuery(id+"F27.boolean.opBoolean","SPLIT",FACE,{"disambiguationData":[TD([makeQuery(id+"F27.opExtrude","SWEPT_FACE",FACE,{"disambiguationData":[OSD([sQuery(id+"F26.wireOp",EDGE,"E46.14.0")])]})])],"derivedFrom":makeQuery(id+"F25.opExtrude","CAP_FACE",FACE,{"disambiguationData":[OSD([sQuery(id+"F24.wireOp",EDGE,"E42")])],"isStart":true})});
            var Q25;
            Q25=makeQuery(id+"F27.boolean.opBoolean","SPLIT",FACE,{"disambiguationData":[TD([makeQuery(id+"F27.opExtrude","SWEPT_FACE",FACE,{"disambiguationData":[OSD([sQuery(id+"F26.wireOp",EDGE,"E46.12.0")])]})])],"derivedFrom":makeQuery(id+"F25.opExtrude","CAP_FACE",FACE,{"disambiguationData":[OSD([sQuery(id+"F24.wireOp",EDGE,"E42")])],"isStart":true})});
            var Q26;
            Q26=makeQuery(id+"F27.boolean.opBoolean","SPLIT",FACE,{"disambiguationData":[TD([makeQuery(id+"F27.opExtrude","SWEPT_FACE",FACE,{"disambiguationData":[OSD([sQuery(id+"F26.wireOp",EDGE,"E46.11.0")])]})])],"derivedFrom":makeQuery(id+"F25.opExtrude","CAP_FACE",FACE,{"disambiguationData":[OSD([sQuery(id+"F24.wireOp",EDGE,"E42")])],"isStart":true})});
            var Q27;
            Q27=makeQuery(id+"F27.boolean.opBoolean","SPLIT",FACE,{"disambiguationData":[TD([makeQuery(id+"F27.opExtrude","SWEPT_FACE",FACE,{"disambiguationData":[OSD([sQuery(id+"F26.wireOp",EDGE,"E46.10.0")])]})])],"derivedFrom":makeQuery(id+"F25.opExtrude","CAP_FACE",FACE,{"disambiguationData":[OSD([sQuery(id+"F24.wireOp",EDGE,"E42")])],"isStart":true})});
            var Q28;
            Q28=makeQuery(id+"F27.boolean.opBoolean","SPLIT",FACE,{"disambiguationData":[TD([makeQuery(id+"F27.opExtrude","SWEPT_FACE",FACE,{"disambiguationData":[OSD([sQuery(id+"F26.wireOp",EDGE,"E46.9.0")])]})])],"derivedFrom":makeQuery(id+"F25.opExtrude","CAP_FACE",FACE,{"disambiguationData":[OSD([sQuery(id+"F24.wireOp",EDGE,"E42")])],"isStart":true})});
            var Q29;
            Q29=makeQuery(id+"F27.boolean.opBoolean","SPLIT",FACE,{"disambiguationData":[TD([makeQuery(id+"F27.opExtrude","SWEPT_FACE",FACE,{"disambiguationData":[OSD([sQuery(id+"F26.wireOp",EDGE,"E47")])]})])],"derivedFrom":makeQuery(id+"F25.opExtrude","CAP_FACE",FACE,{"disambiguationData":[OSD([sQuery(id+"F24.wireOp",EDGE,"E42")])],"isStart":true})});
            var Q30;
            Q30=makeQuery(id+"F27.boolean.opBoolean","SPLIT",FACE,{"disambiguationData":[TD([makeQuery(id+"F27.opExtrude","SWEPT_FACE",FACE,{"disambiguationData":[OSD([sQuery(id+"F26.wireOp",EDGE,"E49.18.0")])]})])],"derivedFrom":makeQuery(id+"F25.opExtrude","CAP_FACE",FACE,{"disambiguationData":[OSD([sQuery(id+"F24.wireOp",EDGE,"E42")])],"isStart":true})});
            var Q31;
            Q31=makeQuery(id+"F27.boolean.opBoolean","SPLIT",FACE,{"disambiguationData":[TD([makeQuery(id+"F27.opExtrude","SWEPT_FACE",FACE,{"disambiguationData":[OSD([sQuery(id+"F26.wireOp",EDGE,"E49.17.0")])]})])],"derivedFrom":makeQuery(id+"F25.opExtrude","CAP_FACE",FACE,{"disambiguationData":[OSD([sQuery(id+"F24.wireOp",EDGE,"E42")])],"isStart":true})});
            var Q32;
            Q32=makeQuery(id+"F27.boolean.opBoolean","SPLIT",FACE,{"disambiguationData":[TD([makeQuery(id+"F27.opExtrude","SWEPT_FACE",FACE,{"disambiguationData":[OSD([sQuery(id+"F26.wireOp",EDGE,"E49.16.0")])]})])],"derivedFrom":makeQuery(id+"F25.opExtrude","CAP_FACE",FACE,{"disambiguationData":[OSD([sQuery(id+"F24.wireOp",EDGE,"E42")])],"isStart":true})});
            var Q33;
            Q33=makeQuery(id+"F27.boolean.opBoolean","SPLIT",FACE,{"disambiguationData":[TD([makeQuery(id+"F27.opExtrude","SWEPT_FACE",FACE,{"disambiguationData":[OSD([sQuery(id+"F26.wireOp",EDGE,"E49.15.0")])]})])],"derivedFrom":makeQuery(id+"F25.opExtrude","CAP_FACE",FACE,{"disambiguationData":[OSD([sQuery(id+"F24.wireOp",EDGE,"E42")])],"isStart":true})});
            var Q34;
            Q34=makeQuery(id+"F27.boolean.opBoolean","SPLIT",FACE,{"disambiguationData":[TD([makeQuery(id+"F27.opExtrude","SWEPT_FACE",FACE,{"disambiguationData":[OSD([sQuery(id+"F26.wireOp",EDGE,"E49.14.0")])]})])],"derivedFrom":makeQuery(id+"F25.opExtrude","CAP_FACE",FACE,{"disambiguationData":[OSD([sQuery(id+"F24.wireOp",EDGE,"E42")])],"isStart":true})});
            var Q35;
            Q35=makeQuery(id+"F27.boolean.opBoolean","SPLIT",FACE,{"disambiguationData":[TD([makeQuery(id+"F27.opExtrude","SWEPT_FACE",FACE,{"disambiguationData":[OSD([sQuery(id+"F26.wireOp",EDGE,"E49.13.0")])]})])],"derivedFrom":makeQuery(id+"F25.opExtrude","CAP_FACE",FACE,{"disambiguationData":[OSD([sQuery(id+"F24.wireOp",EDGE,"E42")])],"isStart":true})});
            var Q36;
            Q36=makeQuery(id+"F27.boolean.opBoolean","SPLIT",FACE,{"disambiguationData":[TD([makeQuery(id+"F27.opExtrude","SWEPT_FACE",FACE,{"disambiguationData":[OSD([sQuery(id+"F26.wireOp",EDGE,"E49.12.0")])]})])],"derivedFrom":makeQuery(id+"F25.opExtrude","CAP_FACE",FACE,{"disambiguationData":[OSD([sQuery(id+"F24.wireOp",EDGE,"E42")])],"isStart":true})});
            var Q37;
            Q37=makeQuery(id+"F27.boolean.opBoolean","SPLIT",FACE,{"disambiguationData":[TD([makeQuery(id+"F27.opExtrude","SWEPT_FACE",FACE,{"disambiguationData":[OSD([sQuery(id+"F26.wireOp",EDGE,"E49.11.0")])]})])],"derivedFrom":makeQuery(id+"F25.opExtrude","CAP_FACE",FACE,{"disambiguationData":[OSD([sQuery(id+"F24.wireOp",EDGE,"E42")])],"isStart":true})});
            var Q38;
            Q38=makeQuery(id+"F27.boolean.opBoolean","SPLIT",FACE,{"disambiguationData":[TD([makeQuery(id+"F27.opExtrude","SWEPT_FACE",FACE,{"disambiguationData":[OSD([sQuery(id+"F26.wireOp",EDGE,"E49.10.0")])]})])],"derivedFrom":makeQuery(id+"F25.opExtrude","CAP_FACE",FACE,{"disambiguationData":[OSD([sQuery(id+"F24.wireOp",EDGE,"E42")])],"isStart":true})});
            var Q39;
            Q39=makeQuery(id+"F27.boolean.opBoolean","SPLIT",FACE,{"disambiguationData":[TD([makeQuery(id+"F27.opExtrude","SWEPT_FACE",FACE,{"disambiguationData":[OSD([sQuery(id+"F26.wireOp",EDGE,"E49.9.0")])]})])],"derivedFrom":makeQuery(id+"F25.opExtrude","CAP_FACE",FACE,{"disambiguationData":[OSD([sQuery(id+"F24.wireOp",EDGE,"E42")])],"isStart":true})});
            var Q40;
            Q40=makeQuery(id+"F27.boolean.opBoolean","SPLIT",FACE,{"disambiguationData":[TD([makeQuery(id+"F27.opExtrude","SWEPT_FACE",FACE,{"disambiguationData":[OSD([sQuery(id+"F26.wireOp",EDGE,"E49.8.0")])]})])],"derivedFrom":makeQuery(id+"F25.opExtrude","CAP_FACE",FACE,{"disambiguationData":[OSD([sQuery(id+"F24.wireOp",EDGE,"E42")])],"isStart":true})});
            var Q41;
            Q41=makeQuery(id+"F27.boolean.opBoolean","SPLIT",FACE,{"disambiguationData":[TD([makeQuery(id+"F27.opExtrude","SWEPT_FACE",FACE,{"disambiguationData":[OSD([sQuery(id+"F26.wireOp",EDGE,"E49.7.0")])]})])],"derivedFrom":makeQuery(id+"F25.opExtrude","CAP_FACE",FACE,{"disambiguationData":[OSD([sQuery(id+"F24.wireOp",EDGE,"E42")])],"isStart":true})});
            var Q42;
            Q42=makeQuery(id+"F27.boolean.opBoolean","SPLIT",FACE,{"disambiguationData":[TD([makeQuery(id+"F27.opExtrude","SWEPT_FACE",FACE,{"disambiguationData":[OSD([sQuery(id+"F26.wireOp",EDGE,"E49.5.0")])]})])],"derivedFrom":makeQuery(id+"F25.opExtrude","CAP_FACE",FACE,{"disambiguationData":[OSD([sQuery(id+"F24.wireOp",EDGE,"E42")])],"isStart":true})});
            var Q43;
            Q43=makeQuery(id+"F27.boolean.opBoolean","SPLIT",FACE,{"disambiguationData":[TD([makeQuery(id+"F27.opExtrude","SWEPT_FACE",FACE,{"disambiguationData":[OSD([sQuery(id+"F26.wireOp",EDGE,"E49.4.0")])]})])],"derivedFrom":makeQuery(id+"F25.opExtrude","CAP_FACE",FACE,{"disambiguationData":[OSD([sQuery(id+"F24.wireOp",EDGE,"E42")])],"isStart":true})});
            var Q44;
            Q44=makeQuery(id+"F27.boolean.opBoolean","SPLIT",FACE,{"disambiguationData":[TD([makeQuery(id+"F27.opExtrude","SWEPT_FACE",FACE,{"disambiguationData":[OSD([sQuery(id+"F26.wireOp",EDGE,"E49.6.0")])]})])],"derivedFrom":makeQuery(id+"F25.opExtrude","CAP_FACE",FACE,{"disambiguationData":[OSD([sQuery(id+"F24.wireOp",EDGE,"E42")])],"isStart":true})});
            var Q45;
            Q45=makeQuery(id+"F27.boolean.opBoolean","SPLIT",FACE,{"disambiguationData":[TD([makeQuery(id+"F27.opExtrude","SWEPT_FACE",FACE,{"disambiguationData":[OSD([sQuery(id+"F26.wireOp",EDGE,"E49.3.0")])]})])],"derivedFrom":makeQuery(id+"F25.opExtrude","CAP_FACE",FACE,{"disambiguationData":[OSD([sQuery(id+"F24.wireOp",EDGE,"E42")])],"isStart":true})});
            var Q46;
            Q46=makeQuery(id+"F27.boolean.opBoolean","SPLIT",FACE,{"disambiguationData":[TD([makeQuery(id+"F27.opExtrude","SWEPT_FACE",FACE,{"disambiguationData":[OSD([sQuery(id+"F26.wireOp",EDGE,"E49.2.0")])]})])],"derivedFrom":makeQuery(id+"F25.opExtrude","CAP_FACE",FACE,{"disambiguationData":[OSD([sQuery(id+"F24.wireOp",EDGE,"E42")])],"isStart":true})});
            var Q47;
            Q47=makeQuery(id+"F27.boolean.opBoolean","SPLIT",FACE,{"disambiguationData":[TD([makeQuery(id+"F27.opExtrude","SWEPT_FACE",FACE,{"disambiguationData":[OSD([sQuery(id+"F26.wireOp",EDGE,"E49.1.0")])]})])],"derivedFrom":makeQuery(id+"F25.opExtrude","CAP_FACE",FACE,{"disambiguationData":[OSD([sQuery(id+"F24.wireOp",EDGE,"E42")])],"isStart":true})});
            var Q48;
            Q48=makeQuery(id+"F27.boolean.opBoolean","SPLIT",FACE,{"disambiguationData":[TD([makeQuery(id+"F27.opExtrude","SWEPT_FACE",FACE,{"disambiguationData":[OSD([sQuery(id+"F26.wireOp",EDGE,"E50.9.0")])]})])],"derivedFrom":makeQuery(id+"F25.opExtrude","CAP_FACE",FACE,{"disambiguationData":[OSD([sQuery(id+"F24.wireOp",EDGE,"E42")])],"isStart":true})});
            var Q49;
            Q49=makeQuery(id+"F27.boolean.opBoolean","SPLIT",FACE,{"disambiguationData":[TD([makeQuery(id+"F27.opExtrude","SWEPT_FACE",FACE,{"disambiguationData":[OSD([sQuery(id+"F26.wireOp",EDGE,"E50.8.0")])]})])],"derivedFrom":makeQuery(id+"F25.opExtrude","CAP_FACE",FACE,{"disambiguationData":[OSD([sQuery(id+"F24.wireOp",EDGE,"E42")])],"isStart":true})});
            var Q50;
            Q50=makeQuery(id+"F27.boolean.opBoolean","SPLIT",FACE,{"disambiguationData":[TD([makeQuery(id+"F27.opExtrude","SWEPT_FACE",FACE,{"disambiguationData":[OSD([sQuery(id+"F26.wireOp",EDGE,"E49.19.0")])]})])],"derivedFrom":makeQuery(id+"F25.opExtrude","CAP_FACE",FACE,{"disambiguationData":[OSD([sQuery(id+"F24.wireOp",EDGE,"E42")])],"isStart":true})});
            var Q51;
            Q51=makeQuery(id+"F27.boolean.opBoolean","SPLIT",FACE,{"disambiguationData":[TD([makeQuery(id+"F27.opExtrude","SWEPT_FACE",FACE,{"disambiguationData":[OSD([sQuery(id+"F26.wireOp",EDGE,"E50.5.0")])]})])],"derivedFrom":makeQuery(id+"F25.opExtrude","CAP_FACE",FACE,{"disambiguationData":[OSD([sQuery(id+"F24.wireOp",EDGE,"E42")])],"isStart":true})});
            var Q52;
            Q52=makeQuery(id+"F27.boolean.opBoolean","SPLIT",FACE,{"disambiguationData":[TD([makeQuery(id+"F27.opExtrude","SWEPT_FACE",FACE,{"disambiguationData":[OSD([sQuery(id+"F26.wireOp",EDGE,"E50.4.0")])]})])],"derivedFrom":makeQuery(id+"F25.opExtrude","CAP_FACE",FACE,{"disambiguationData":[OSD([sQuery(id+"F24.wireOp",EDGE,"E42")])],"isStart":true})});
            var Q53;
            Q53=makeQuery(id+"F27.boolean.opBoolean","SPLIT",FACE,{"disambiguationData":[TD([makeQuery(id+"F27.opExtrude","SWEPT_FACE",FACE,{"disambiguationData":[OSD([sQuery(id+"F26.wireOp",EDGE,"E50.3.0")])]})])],"derivedFrom":makeQuery(id+"F25.opExtrude","CAP_FACE",FACE,{"disambiguationData":[OSD([sQuery(id+"F24.wireOp",EDGE,"E42")])],"isStart":true})});
            var Q54;
            Q54=makeQuery(id+"F27.boolean.opBoolean","SPLIT",FACE,{"disambiguationData":[TD([makeQuery(id+"F27.opExtrude","SWEPT_FACE",FACE,{"disambiguationData":[OSD([sQuery(id+"F26.wireOp",EDGE,"E50.2.0")])]})])],"derivedFrom":makeQuery(id+"F25.opExtrude","CAP_FACE",FACE,{"disambiguationData":[OSD([sQuery(id+"F24.wireOp",EDGE,"E42")])],"isStart":true})});
            var Q55;
            Q55=makeQuery(id+"F27.boolean.opBoolean","SPLIT",FACE,{"disambiguationData":[TD([makeQuery(id+"F27.opExtrude","SWEPT_FACE",FACE,{"disambiguationData":[OSD([sQuery(id+"F26.wireOp",EDGE,"E50.1.0")])]})])],"derivedFrom":makeQuery(id+"F25.opExtrude","CAP_FACE",FACE,{"disambiguationData":[OSD([sQuery(id+"F24.wireOp",EDGE,"E42")])],"isStart":true})});
            var Q56;
            Q56=makeQuery(id+"F27.boolean.opBoolean","SPLIT",FACE,{"disambiguationData":[TD([makeQuery(id+"F27.opExtrude","SWEPT_FACE",FACE,{"disambiguationData":[OSD([sQuery(id+"F26.wireOp",EDGE,"E48")])]})])],"derivedFrom":makeQuery(id+"F25.opExtrude","CAP_FACE",FACE,{"disambiguationData":[OSD([sQuery(id+"F24.wireOp",EDGE,"E42")])],"isStart":true})});
            var Q57;
            Q57=makeQuery(id+"F27.boolean.opBoolean","SPLIT",FACE,{"disambiguationData":[TD([makeQuery(id+"F27.opExtrude","SWEPT_FACE",FACE,{"disambiguationData":[OSD([sQuery(id+"F26.wireOp",EDGE,"E50.6.0")])]})])],"derivedFrom":makeQuery(id+"F25.opExtrude","CAP_FACE",FACE,{"disambiguationData":[OSD([sQuery(id+"F24.wireOp",EDGE,"E42")])],"isStart":true})});
            var Q58;
            Q58=makeQuery(id+"F27.boolean.opBoolean","SPLIT",FACE,{"disambiguationData":[TD([makeQuery(id+"F27.opExtrude","SWEPT_FACE",FACE,{"disambiguationData":[OSD([sQuery(id+"F26.wireOp",EDGE,"E50.7.0")])]})])],"derivedFrom":makeQuery(id+"F25.opExtrude","CAP_FACE",FACE,{"disambiguationData":[OSD([sQuery(id+"F24.wireOp",EDGE,"E42")])],"isStart":true})});
            var Q59;
            Q59=makeQuery(id+"F27.boolean.opBoolean","SPLIT",FACE,{"disambiguationData":[TD([makeQuery(id+"F27.opExtrude","SWEPT_FACE",FACE,{"disambiguationData":[OSD([sQuery(id+"F26.wireOp",EDGE,"E46.13.0")])]})])],"derivedFrom":makeQuery(id+"F25.opExtrude","CAP_FACE",FACE,{"disambiguationData":[OSD([sQuery(id+"F24.wireOp",EDGE,"E42")])],"isStart":true})});
            extrude(context, id + "F28", {"entities" : qUnion([Q0, Q1, Q2, Q3, Q4, Q5, Q6, Q7, Q8, Q9, Q10, Q11, Q12, Q13, Q14, Q15, Q16, Q17, Q18, Q19, Q20, Q21, Q22, Q23, Q24, Q25, Q26, Q27, Q28, Q29, Q30, Q31, Q32, Q33, Q34, Q35, Q36, Q37, Q38, Q39, Q40, Q41, Q42, Q43, Q44, Q45, Q46, Q47, Q48, Q49, Q50, Q51, Q52, Q53, Q54, Q55, Q56, Q57, Q58, Q59]), "operationType" : NewBodyOperationType.REMOVE, "oppositeDirection" : true, "depth" : 25 * mm, "offsetDistance" : 25 * mm});
        }
    });
